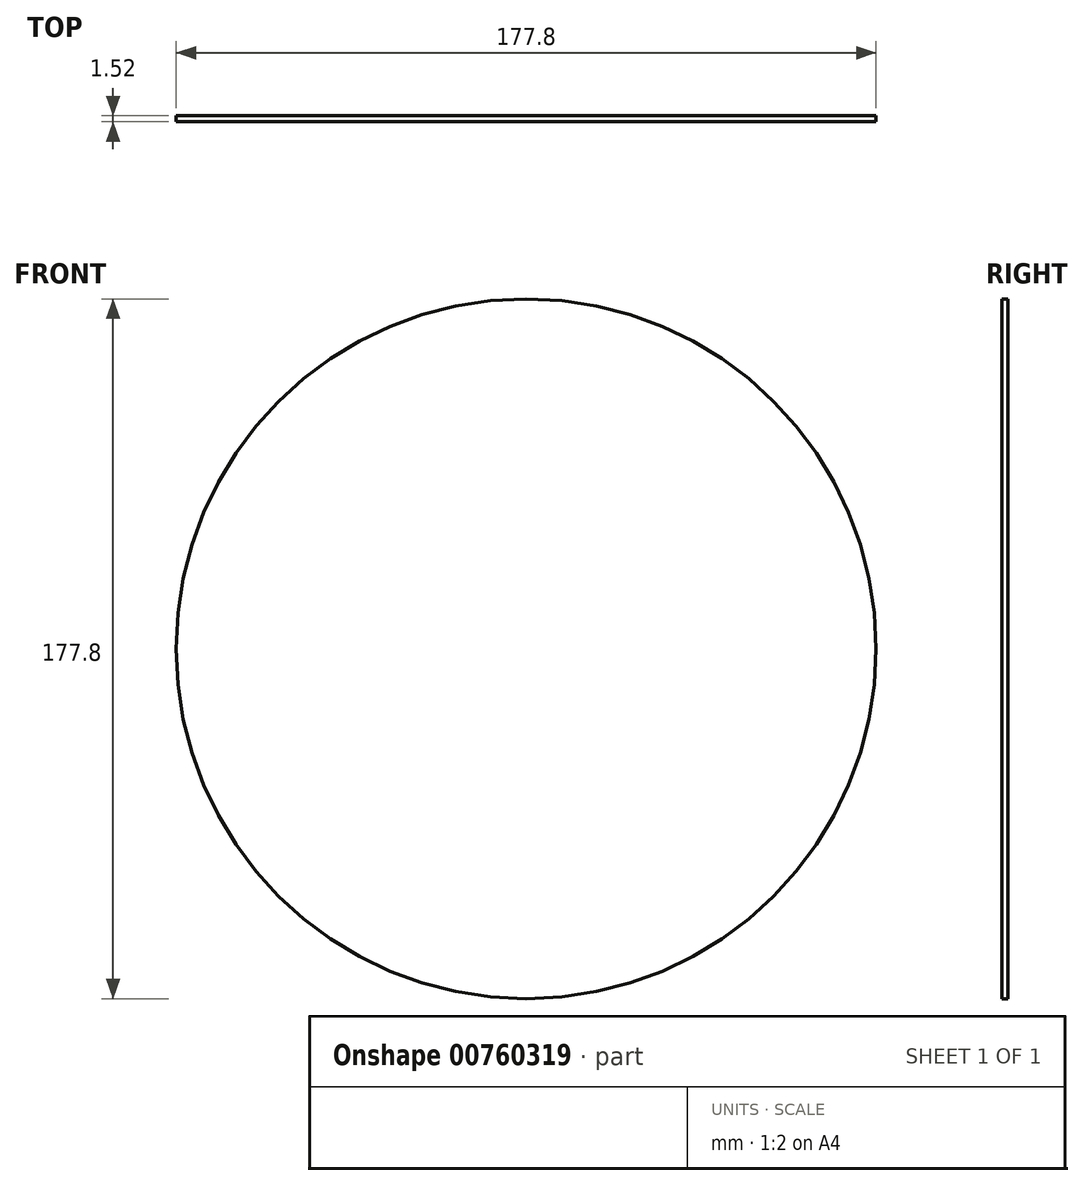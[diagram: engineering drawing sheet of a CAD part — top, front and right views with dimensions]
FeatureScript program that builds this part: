
annotation { "Feature Type Name" : "Feature", "Feature Type Description" : "" }
export const myFeature = defineFeature(function(context is Context, id is Id, definition is map)
    precondition{}
    {
        {
            var Q0;
            Q0=qCreatedBy(makeId("Front.planeOp"),FACE);
            var sketch = newSketch(context, id + "F0", { "sketchPlane" : qUnion([Q0])});
            skCircle(sketch, "E0", {"center": v(0, 0) * mm, "radius": 88.9 * mm});
            skSolve(sketch);
        }
        {
            var Q0;
            Q0 = qSketchRegion(id + "F0", true);
            extrude(context, id + "F1", {"entities" : qUnion([Q0]), "depth" : 1.52 * mm, "offsetDistance" : 25.4 * mm});
        }
    });
